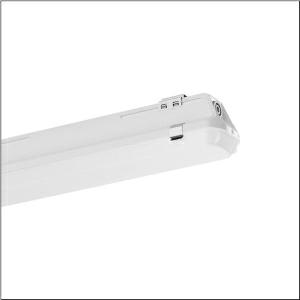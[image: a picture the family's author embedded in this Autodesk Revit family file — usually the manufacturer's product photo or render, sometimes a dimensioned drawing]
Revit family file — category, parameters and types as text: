
# Revit family: monsun_r__11_51fp10fp460h_036e
name_source: partatom
category: Lighting Fixtures
units: mm (PartAtom-declared; Revit-internal decimal feet)

## family parameters
Cut with Voids When Loaded = No
Host = Face
Light Source = No
Part Type = Normal
Room Calculation Point = No
Round Connector Dimension = Use Diameter
Shared = No

## types (1)
- --- (1 x LED, 6050 lm, 34.6 W, 4000K)
    Apparent Load = 35 VA
    CIE Flux Codes = 47 77 93 94 100
    Color Rendering = 80
    Color Temperature = 4000K
    Default Elevation = 1800 mm
    Description = Monsun® 11, damp-proof luminaire, chain hanger, primary optical cover: enclosure, of PMMA, light emission: direct distribution, primary light characteristic: symmetric, installation type: suspended mounting, surface-mounted, horizontal mounting, vertical mounting, LED, rated luminous flux: 6.050lm, luminous efficacy: 175lm/W, light colour: 840, colour temperature: 4000K, control gear: ECG DALI, with terminal, 5-pole, max. 2.5mm², mains connection: 220..240V, AC, 50/60Hz, start of lifetime: 35W, end of service life: 39W, luminaire housing, of glass-fibre reinforced polyester, uncoated, bright grey, incl. chain hanger, length: 1.590mm, width: 90mm, height: 88mm, clip for enclosure, of stainless steel (V2A), ceiling mounting element, of stainless steel (V2A), chain hanger, of stainless steel (V2A), protection rating (complete): IP66, insulation class (complete): insulation class I (protective earthing), certification: CE, ENEC, VDE, UKCA, protection symbol: D, impact resistance: IK04, permissible operating ambient temperature: -25..+40°C, standard: EN 50419, EN 60598-2-1, no direct snow, no direct sun, no direct rain, for indoor or canopied outdoor use, corresponds to IFS (International Featured Standards) requirements for safety and quality in the food industry, contact your sales advisor before using the luminaires in applications with unclear chemical exposure, large temperature fluctuations or condensation-forming humidity, LABS conformity tested according to VDMA 24364:2018-05, packaging unit: 1 piece
    Height = 89 mm
    Lamp = 1 x LED
    Lamp Light Flux = 6050 lm
    Lamp Power = 34.6 W
    Lamp count = 1
    Length = 1590 mm
    Luminous efficacy = 175 lm/W
    Manufacturer = Siteco
    ModVariant = No
    Model = 51FP10FP460H
    Mounting Place = Ceiling
    Mounting Type = Surface mounted
    Number of Poles = 1
    OnlyDefault = Yes
    Power Factor = 1
    Product Name = Monsun® 11
    Product group = damp-proof luminaire
    ProductGroupID = 300
    Protection Class = Protection class I
    Protection Degree = IP 66
    RLX_Detail_Level = 1
    RLX_Emergency_Light_Flux = 0 lm
    RLX_Emergency_Type = 0
    RLX_Emergency_Type_DB = No
    RlxData = <blob elided: 92089 chars, md5=d1022500>
    Socket = socket
    Standby Power = 0 W
    System Light Flux = 6050 lm
    System Power = 35 W
    Type Comments = factory setting: luminous flux: 100 % | dim-lin: 254 | 232 mA
    Type Image = l_1319650.jpg
    URL = http://relux.com
    VarID = @adj_174899
    Voltage = 0 V
    Weight = 0.00 kg
    Width = 90 mm

## geometry (parser evidence)
native form markers: Blend x4, Sweep x14
no freeform markers — native parametric forms only
